# Revit family: ledwall-mounted-e2_rd275-22w_522020001600
name_source: partatom
category: Leuchten
revit_build: Autodesk Revit 2016 (Build: 20190508_0715(x64)
units: mm (PartAtom-declared; Revit-internal decimal feet)

## family parameters
Basisbauteil = Fläche
Beim Laden mit Abzugskörper schneiden = Nein
Bemaßung runder Anschluss = Durchmesser verwenden
Gemeinsam genutzt = Nein
Lichtquelle = Nein
Raumberechnungspunkt = Nein
Teiletyp = Normal

## types (1)
- LEDWall-Mounted-E2 Rd275-22W (1 x LED, 2500 lm)
    Approval mark = CE
    Beschreibung = Stylish, compact and sturdy wall mounted fixture (IP54+IK08). Easy wiring with through-wiring possibility. Integrated CCT switch for color selection (3000K-4000K). Energy savings up to 60% compared to compact fluorescent based fixtures.
    CIE Flux Codes = 44 74 93 96 100
    Control Gear = Electronic ballast
    Height = 71 mm
    Hersteller = OPPLE
    Lamp Light Flux = 2500 lm
    Lamp count = 1
    Lampe = 1 x LED
    Length = 275 mm
    Luminous efficacy = 114 lm/W
    ModVariant = Nein
    Modell = 522020001600
    Mounting Place = Wall
    Mounting Type = Surface mounted
    Number of Poles = 1
    OnlyDefault = Ja
    Power Factor = 1
    Product Name = LEDWall-Mounted-E2 Rd275-22W
    Product group = Wall-Mounted EcoMax G2
    ProductGroupID = 2021
    Protection Class = Protection class II
    Protection Degree = IP 54
    RLX_Detail_Level = 1
    RlxData = <blob elided: 131161 chars, md5=71ac94fc>
    Scheinlast = 22 VA
    Socket = socket
    Standby Power = 0 W
    System Light Flux = 2500 lm
    System Power = 22 W
    Typenbild = 522020001600.jpg
    Typenkommentare = Product without accessories
    URL = http://relux.com
    VarID = ---
    Voltage = 0 V
    Vorgabe-Ansicht = 1800 mm
    Weight = 0.00 kg
    Width = 0 mm  [stored 0 ft]

note: [stored X ft] marks values corroborated as IEEE doubles in the binary element streams (Revit-internal decimal feet)

## geometry (parser evidence)
native form markers: Blend x4, Sweep x10
no freeform markers — native parametric forms only
